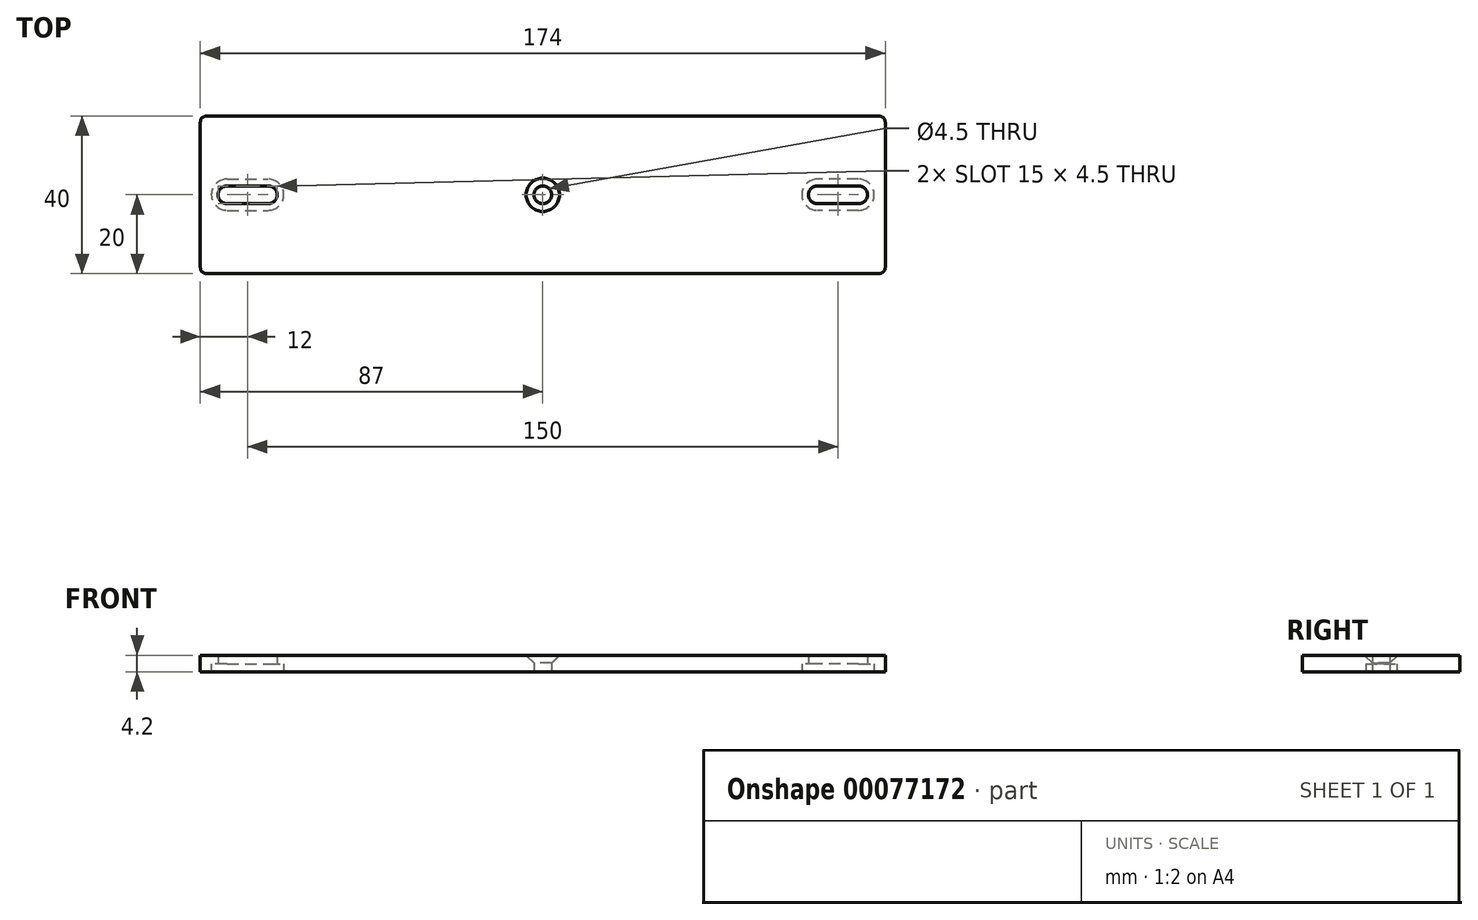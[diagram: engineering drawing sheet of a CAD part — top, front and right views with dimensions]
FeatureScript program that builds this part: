
annotation { "Feature Type Name" : "Feature", "Feature Type Description" : "" }
export const myFeature = defineFeature(function(context is Context, id is Id, definition is map)
    precondition{}
    {
        {
            var Q0;
            Q0=qCreatedBy(makeId("Top.planeOp"),FACE);
            var sketch = newSketch(context, id + "F0", { "sketchPlane" : qUnion([Q0])});
            skLineSegment(sketch, "E0.bottom", {"start": v(0, 0) * mm, "end": v(174, 0) * mm});
            skLineSegment(sketch, "E0.top", {"start": v(0, 40) * mm, "end": v(174, 40) * mm});
            skLineSegment(sketch, "E0.left", {"start": v(0, 0) * mm, "end": v(0, 40) * mm});
            skLineSegment(sketch, "E0.right", {"start": v(174, 0) * mm, "end": v(174, 40) * mm});
            skLineSegment(sketch, "E1.bottom", {"start": v(6.75, 22.25) * mm, "end": v(17.25, 22.25) * mm});
            skLineSegment(sketch, "E1.top", {"start": v(6.75, 17.75) * mm, "end": v(17.25, 17.75) * mm});
            skLineSegment(sketch, "E1.left", {"start": v(4.5, 20) * mm, "end": v(4.5, 20) * mm});
            skLineSegment(sketch, "E1.right", {"start": v(19.5, 20) * mm, "end": v(19.5, 20) * mm});
            skLineSegment(sketch, "E2.bottom", {"start": v(167.25, 22.25) * mm, "end": v(156.75, 22.25) * mm});
            skLineSegment(sketch, "E2.top", {"start": v(167.25, 17.75) * mm, "end": v(156.75, 17.75) * mm});
            skLineSegment(sketch, "E2.left", {"start": v(169.5, 20) * mm, "end": v(169.5, 20) * mm});
            skLineSegment(sketch, "E2.right", {"start": v(154.5, 20) * mm, "end": v(154.5, 20) * mm});
            skPoint(sketch, "E3.visualSharp", {"position": v(19.5, 22.25) * mm});
            skArc(sketch, "E3.filletArc", {"start": v(19.5, 20) * mm, "mid": v(18.84, 21.6) * mm, "end": v(17.25, 22.25) * mm});
            skPoint(sketch, "E4.visualSharp", {"position": v(19.5, 17.75) * mm});
            skArc(sketch, "E4.filletArc", {"start": v(17.25, 17.75) * mm, "mid": v(18.84, 18.4) * mm, "end": v(19.5, 20) * mm});
            skPoint(sketch, "E5.visualSharp", {"position": v(4.5, 17.75) * mm});
            skArc(sketch, "E5.filletArc", {"start": v(4.5, 20) * mm, "mid": v(5.16, 18.4) * mm, "end": v(6.75, 17.75) * mm});
            skPoint(sketch, "E6.visualSharp", {"position": v(4.5, 22.25) * mm});
            skArc(sketch, "E6.filletArc", {"start": v(6.75, 22.25) * mm, "mid": v(5.16, 21.6) * mm, "end": v(4.5, 20) * mm});
            skPoint(sketch, "E7.visualSharp", {"position": v(154.5, 22.25) * mm});
            skArc(sketch, "E7.filletArc", {"start": v(156.75, 22.25) * mm, "mid": v(155.16, 21.6) * mm, "end": v(154.5, 20) * mm});
            skPoint(sketch, "E8.visualSharp", {"position": v(154.5, 17.75) * mm});
            skArc(sketch, "E8.filletArc", {"start": v(154.5, 20) * mm, "mid": v(155.16, 18.4) * mm, "end": v(156.75, 17.75) * mm});
            skPoint(sketch, "E9.visualSharp", {"position": v(169.5, 17.75) * mm});
            skArc(sketch, "E9.filletArc", {"start": v(167.25, 17.75) * mm, "mid": v(168.84, 18.4) * mm, "end": v(169.5, 20) * mm});
            skPoint(sketch, "E10.visualSharp", {"position": v(169.5, 22.25) * mm});
            skArc(sketch, "E10.filletArc", {"start": v(169.5, 20) * mm, "mid": v(168.84, 21.6) * mm, "end": v(167.25, 22.25) * mm});
            skCircle(sketch, "E11", {"center": v(87, 20) * mm, "radius": 2.25 * mm});
            skSolve(sketch);
        }
        {
            var Q0;
            Q0=qSketchRegion(id+"F0",true);
            extrude(context, id + "F1", {"entities" : qUnion([Q0]), "depth" : 4.2 * mm});
        }
        {
            var Q0;
            Q0=qCreatedBy(makeId("Top.planeOp"),FACE);
            var sketch = newSketch(context, id + "F2", { "sketchPlane" : qUnion([Q0])});
            skLineSegment(sketch, "E12.0", {"start": v(6.75, 16.05) * mm, "end": v(17.25, 16.05) * mm});
            skArc(sketch, "E12.1", {"start": v(6.75, 23.95) * mm, "mid": v(2.8, 20) * mm, "end": v(6.75, 16.05) * mm});
            skLineSegment(sketch, "E12.2", {"start": v(6.75, 23.95) * mm, "end": v(17.25, 23.95) * mm});
            skArc(sketch, "E12.3", {"start": v(17.25, 16.05) * mm, "mid": v(21.2, 20) * mm, "end": v(17.25, 23.95) * mm});
            skLineSegment(sketch, "E13.0", {"start": v(167.25, 16.05) * mm, "end": v(156.75, 16.05) * mm});
            skArc(sketch, "E13.1", {"start": v(167.25, 16.05) * mm, "mid": v(171.2, 20) * mm, "end": v(167.25, 23.95) * mm});
            skLineSegment(sketch, "E13.2", {"start": v(167.25, 23.95) * mm, "end": v(156.75, 23.95) * mm});
            skArc(sketch, "E13.3", {"start": v(156.75, 23.95) * mm, "mid": v(152.8, 20) * mm, "end": v(156.75, 16.05) * mm});
            skSolve(sketch);
        }
        {
            var Q0;
            Q0=qSketchRegion(id+"F2",true);
            extrude(context, id + "F3", {"entities" : qUnion([Q0]), "operationType" : NewBodyOperationType.REMOVE, "depth" : 2 * mm});
        }
        {
            var Q0;
            Q0=makeQuery(id+"F1.opExtrude","CAP_EDGE",EDGE,{"disambiguationData":[OSD([sQuery(id+"F0.wireOp",EDGE,"E11")])],"isStart":false});
            chamfer(context, id + "F4", {"entities" : qUnion([Q0]), "width" : 2 * mm, "tangentPropagation" : true});
        }
        {
            var Q0;
            Q0=makeQuery(id+"F1.opExtrude","SWEPT_EDGE",EDGE,{"disambiguationData":[OSD([sQuery(id+"F0.wireOp",EDGE,"E0.bottom"),sQuery(id+"F0.wireOp",EDGE,"E0.right")])]});
            var Q1;
            Q1=makeQuery(id+"F1.opExtrude","SWEPT_EDGE",EDGE,{"disambiguationData":[OSD([sQuery(id+"F0.wireOp",EDGE,"E0.top"),sQuery(id+"F0.wireOp",EDGE,"E0.right")])]});
            var Q2;
            Q2=makeQuery(id+"F1.opExtrude","SWEPT_EDGE",EDGE,{"disambiguationData":[OSD([sQuery(id+"F0.wireOp",EDGE,"E0.top"),sQuery(id+"F0.wireOp",EDGE,"E0.left")])]});
            var Q3;
            Q3=makeQuery(id+"F1.opExtrude","SWEPT_EDGE",EDGE,{"disambiguationData":[OSD([sQuery(id+"F0.wireOp",EDGE,"E0.bottom"),sQuery(id+"F0.wireOp",EDGE,"E0.left")])]});
            fillet(context, id + "F5", {"entities" : qUnion([Q0, Q1, Q2, Q3]), "radius" : 1.5 * mm, "tangentPropagation" : true, "allowEdgeOverflow" : false});
        }
    });
